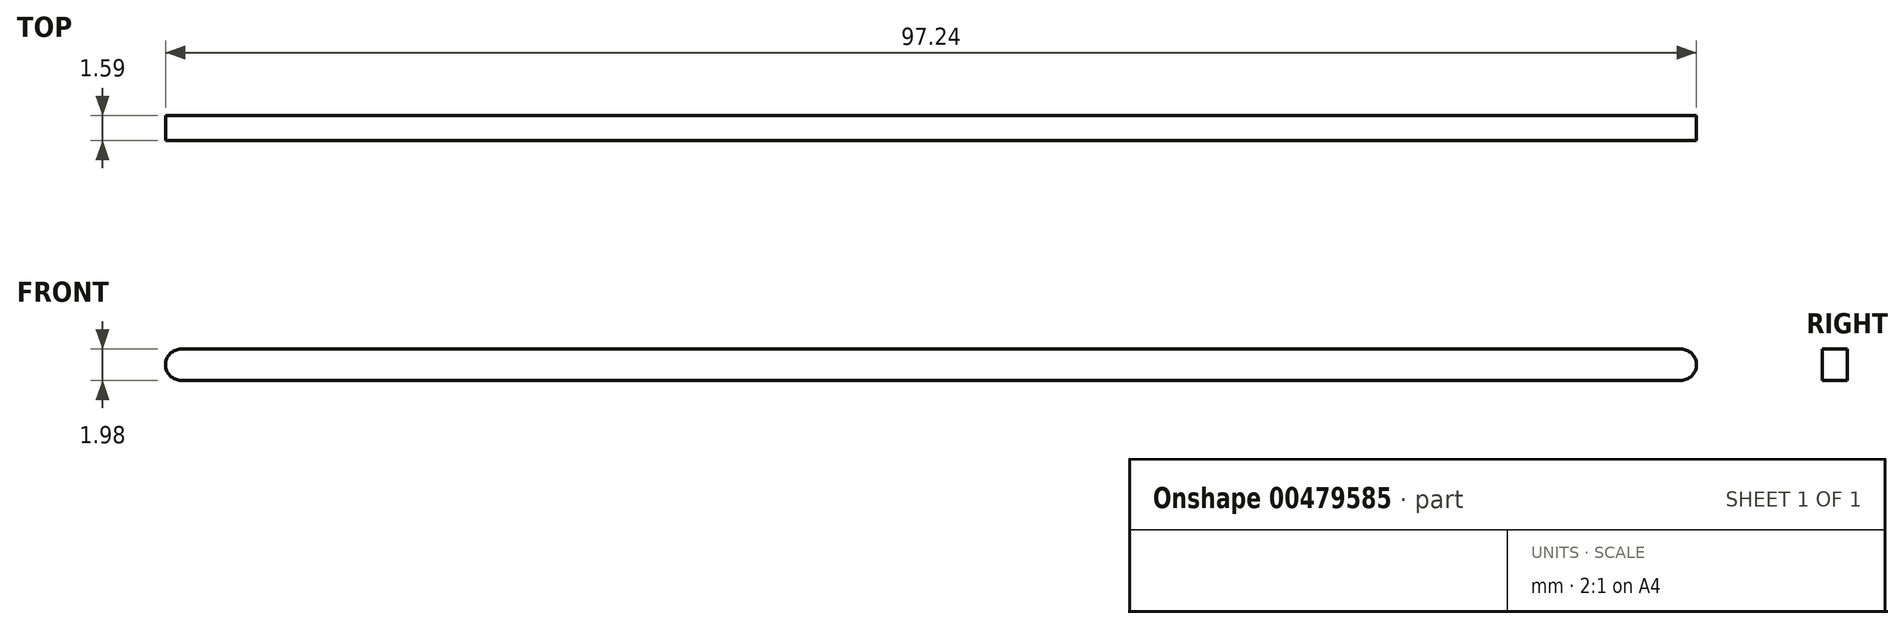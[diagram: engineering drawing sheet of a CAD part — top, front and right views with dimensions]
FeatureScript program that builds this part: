
annotation { "Feature Type Name" : "Feature", "Feature Type Description" : "" }
export const myFeature = defineFeature(function(context is Context, id is Id, definition is map)
    precondition{}
    {
        {
            var Q0;
            Q0=qCreatedBy(makeId("Front.planeOp"),FACE);
            var sketch = newSketch(context, id + "F0", { "sketchPlane" : qUnion([Q0])});
            skLineSegment(sketch, "E0.bottom", {"start": v(47.63, -1) * mm, "end": v(-47.62, -1) * mm});
            skLineSegment(sketch, "E0.top", {"start": v(47.63, 1) * mm, "end": v(-47.62, 1) * mm});
            skPoint(sketch, "E0.middle", {"position": v(0, 0) * mm});
            skArc(sketch, "E1", {"start": v(47.63, -1) * mm, "mid": v(48.62, 0) * mm, "end": v(47.63, 1) * mm});
            skArc(sketch, "E2", {"start": v(-47.62, 1) * mm, "mid": v(-48.62, 0) * mm, "end": v(-47.62, -1) * mm});
            skSolve(sketch);
        }
        {
            var Q0;
            Q0=makeQuery(id+"F0.imprint","IMPRINT",FACE,{"disambiguationData":[TD([[makeQuery(id+"F0.imprint","IMPRINT",EDGE,{"derivedFrom":sQuery(id+"F0.wireOp",EDGE,"E0.bottom")}),-1.0]])]});
            extrude(context, id + "F1", {"entities" : qUnion([Q0]), "depth" : 1.59 * mm});
        }
    });
